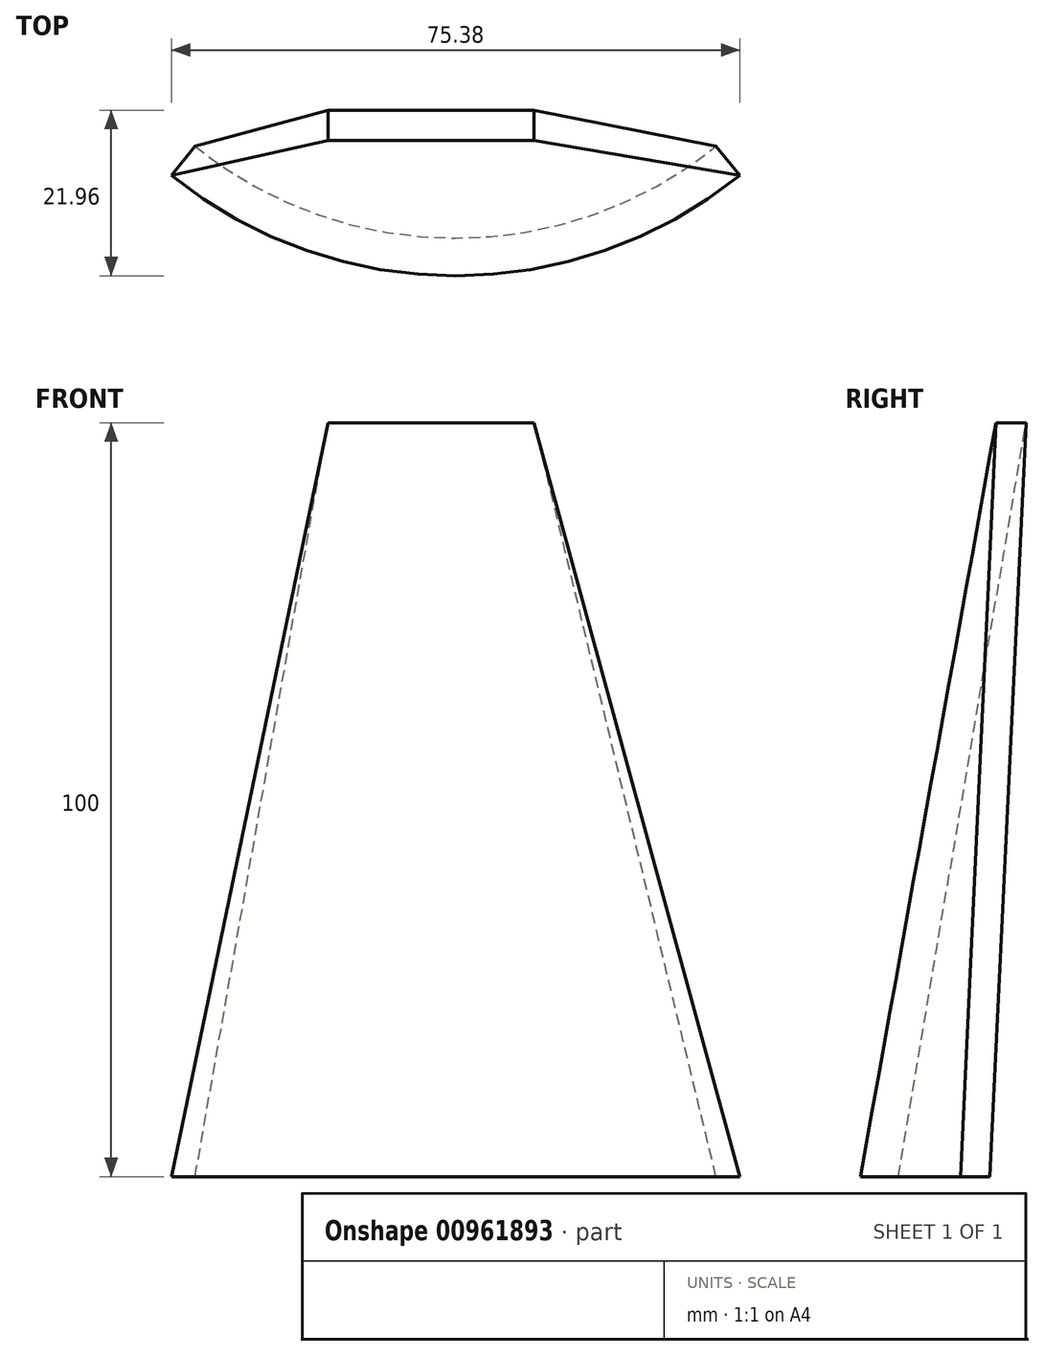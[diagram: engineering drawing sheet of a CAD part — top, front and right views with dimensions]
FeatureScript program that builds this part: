
annotation { "Feature Type Name" : "Feature", "Feature Type Description" : "" }
export const myFeature = defineFeature(function(context is Context, id is Id, definition is map)
    precondition{}
    {
        {
            var Q0;
            Q0=qCreatedBy(makeId("Top.planeOp"),FACE);
            var sketch = newSketch(context, id + "F0", { "sketchPlane" : qUnion([Q0])});
            skArc(sketch, "E0", {"start": v(-37.69, 0) * mm, "mid": v(0, -13.3) * mm, "end": v(37.69, 0) * mm});
            skArc(sketch, "E1.0", {"start": v(-34.55, 3.9) * mm, "mid": v(0, -8.3) * mm, "end": v(34.55, 3.9) * mm});
            skLineSegment(sketch, "E2", {"start": v(-34.55, 3.9) * mm, "end": v(-37.69, 0) * mm});
            skLineSegment(sketch, "E3", {"start": v(34.55, 3.9) * mm, "end": v(37.69, 0) * mm});
            skSolve(sketch);
        }
        {
            var Q0;
            Q0=qCreatedBy(makeId("Top.planeOp"),FACE);
            cPlane(context, id + "F1", {"entities" : qUnion([Q0]), "cplaneType" : CPlaneType.OFFSET, "offset" : 100 * mm, "width" : 150 * mm, "height" : 150 * mm});
        }
        {
            var Q0;
            Q0=qCreatedBy(id+"F1.planeOp",FACE);
            var sketch = newSketch(context, id + "F2", { "sketchPlane" : qUnion([Q0])});
            skLineSegment(sketch, "E4.bottom", {"start": v(10.42, 8.67) * mm, "end": v(-16.94, 8.67) * mm});
            skLineSegment(sketch, "E4.top", {"start": v(10.42, 4.67) * mm, "end": v(-16.94, 4.67) * mm});
            skLineSegment(sketch, "E4.left", {"start": v(10.42, 8.67) * mm, "end": v(10.42, 4.67) * mm});
            skLineSegment(sketch, "E4.right", {"start": v(-16.94, 8.67) * mm, "end": v(-16.94, 4.67) * mm});
            skSolve(sketch);
        }
        {
            var Q0;
            Q0=makeQuery(id+"F0.imprint","IMPRINT",FACE,{"disambiguationData":[TD([[makeQuery(id+"F0.imprint","IMPRINT",EDGE,{"derivedFrom":sQuery(id+"F0.wireOp",EDGE,"E0")}),1.0]])]});
            var Q1;
            Q1=makeQuery(id+"F2.imprint","IMPRINT",FACE,{"disambiguationData":[TD([[makeQuery(id+"F2.imprint","IMPRINT",EDGE,{"derivedFrom":sQuery(id+"F2.wireOp",EDGE,"E4.bottom")}),1.0]])]});
            loft(context, id + "F3", {"sheetProfilesArray" : [{ "sheetProfileEntities" : qUnion([Q0]) }, { "sheetProfileEntities" : qUnion([Q1]) }]});
        }
    });
